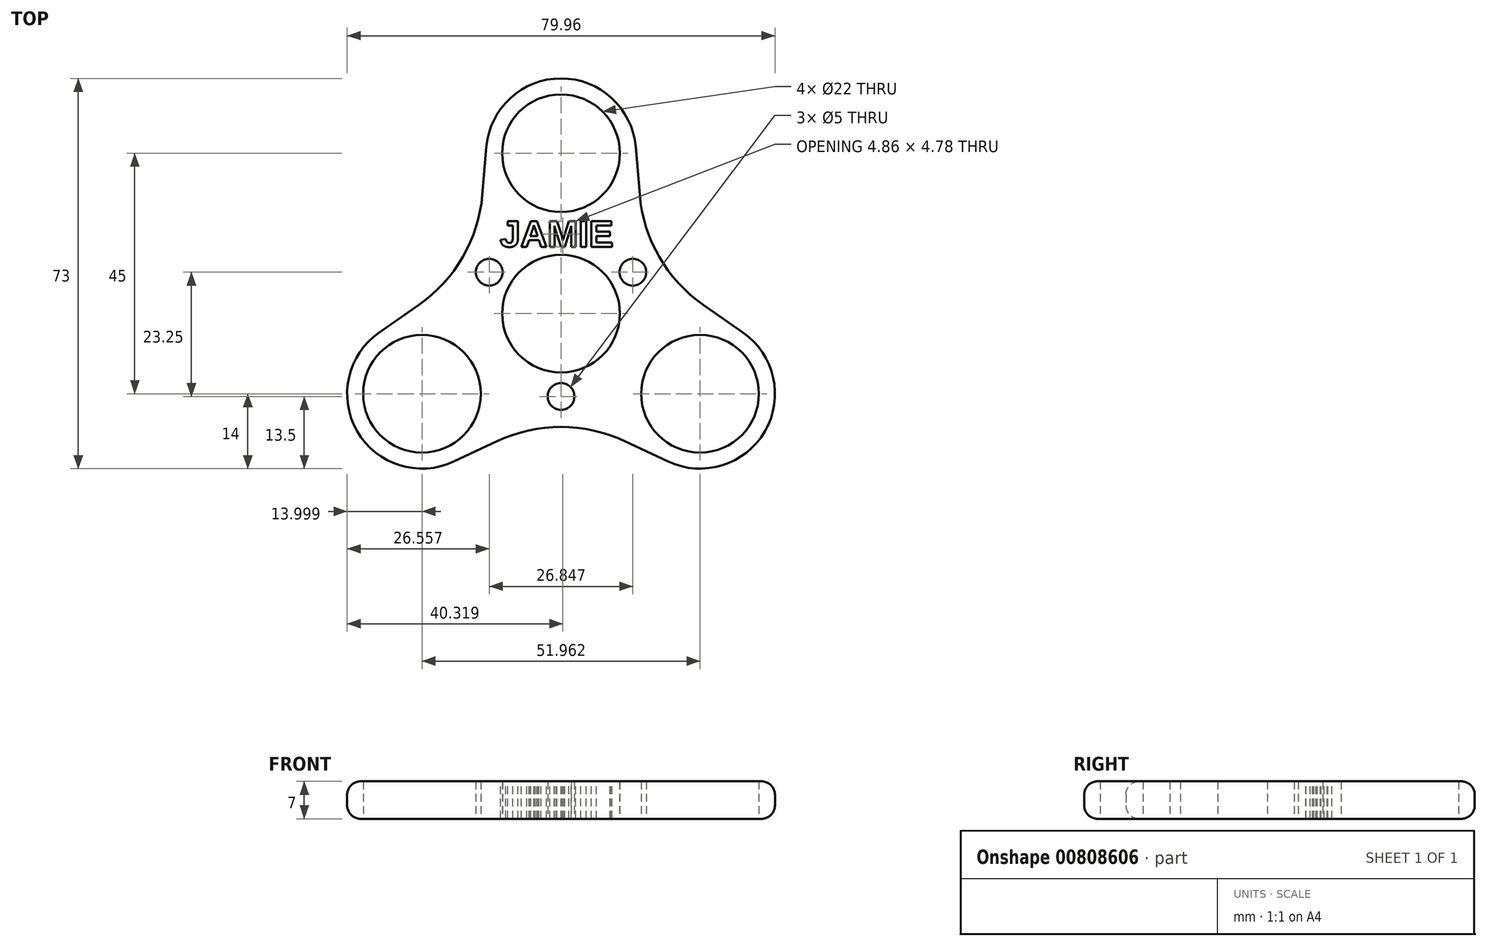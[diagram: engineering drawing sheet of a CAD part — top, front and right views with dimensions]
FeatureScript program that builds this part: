
annotation { "Feature Type Name" : "Feature", "Feature Type Description" : "" }
export const myFeature = defineFeature(function(context is Context, id is Id, definition is map)
    precondition{}
    {
        {
            var Q0;
            Q0=qCreatedBy(makeId("Top.planeOp"),FACE);
            var sketch = newSketch(context, id + "F0", { "sketchPlane" : qUnion([Q0])});
            skCircle(sketch, "E0", {"center": v(0, 0) * mm, "radius": 11 * mm});
            skLineSegment(sketch, "E1", {"start": v(0, 0) * mm, "end": v(0, 30) * mm});
            skCircle(sketch, "E2", {"center": v(0, 30) * mm, "radius": 11 * mm});
            skCircle(sketch, "E3", {"center": v(0, 30) * mm, "radius": 14 * mm});
            skLineSegment(sketch, "E4", {"start": v(0, 0) * mm, "end": v(-25.98, -15) * mm});
            skLineSegment(sketch, "E5", {"start": v(0, 0) * mm, "end": v(25.98, -15) * mm});
            skCircle(sketch, "E6", {"center": v(-25.98, -15) * mm, "radius": 11 * mm});
            skCircle(sketch, "E7", {"center": v(25.98, -15) * mm, "radius": 11 * mm});
            skCircle(sketch, "E8", {"center": v(25.98, -15) * mm, "radius": 14 * mm});
            skCircle(sketch, "E9", {"center": v(-25.98, -15) * mm, "radius": 14 * mm});
            skLineSegment(sketch, "E10", {"start": v(-56.74, -32.28) * mm, "end": v(-57.16, -33) * mm});
            skPoint(sketch, "E11.visualSharp", {"position": v(57.16, -33) * mm});
            skPoint(sketch, "E12.visualSharp", {"position": v(0, 66) * mm});
            skLineSegment(sketch, "E13", {"start": v(0, 0) * mm, "end": v(-13.42, 7.75) * mm});
            skCircle(sketch, "E14", {"center": v(-13.42, 7.75) * mm, "radius": 2.5 * mm});
            skLineSegment(sketch, "E15", {"start": v(-13.42, 7.75) * mm, "end": v(-15.59, 9) * mm});
            skLineSegment(sketch, "E16", {"start": v(-26.61, 1.62) * mm, "end": v(-33.98, -3.5) * mm});
            skLineSegment(sketch, "E17", {"start": v(-13.95, 31.18) * mm, "end": v(-14.7, 22.24) * mm});
            skPoint(sketch, "E18.orphan", {"position": v(-16.59, 0) * mm});
            skArc(sketch, "E19.filletArc", {"start": v(-26.61, 1.62) * mm, "mid": v(-18.36, 10.6) * mm, "end": v(-14.7, 22.24) * mm});
            skLineSegment(sketch, "E20", {"start": v(0, 0) * mm, "end": v(13.42, 7.75) * mm});
            skCircle(sketch, "E21", {"center": v(13.42, 7.75) * mm, "radius": 2.5 * mm});
            skLineSegment(sketch, "E22", {"start": v(13.95, 31.18) * mm, "end": v(14.7, 22.24) * mm});
            skLineSegment(sketch, "E23", {"start": v(33.98, -3.5) * mm, "end": v(26.61, 1.62) * mm});
            skArc(sketch, "E24.filletArc", {"start": v(14.7, 22.24) * mm, "mid": v(18.36, 10.6) * mm, "end": v(26.61, 1.62) * mm});
            skLineSegment(sketch, "E25", {"start": v(0, 0) * mm, "end": v(0, -15.5) * mm});
            skCircle(sketch, "E26", {"center": v(0, -15.5) * mm, "radius": 2.5 * mm});
            skLineSegment(sketch, "E27", {"start": v(-20.03, -27.67) * mm, "end": v(-11.9, -23.86) * mm});
            skLineSegment(sketch, "E28", {"start": v(20.03, -27.67) * mm, "end": v(11.9, -23.86) * mm});
            skArc(sketch, "E29.filletArc", {"start": v(11.9, -23.86) * mm, "mid": v(0, -21.2) * mm, "end": v(-11.9, -23.86) * mm});
            skSolve(sketch);
        }
        {
            var Q0;
            Q0 = qSketchRegion(id + "F0", true);
            extrude(context, id + "F1", {"entities" : qUnion([Q0]), "depth" : 7 * mm, "offsetDistance" : 25 * mm});
        }
        {
            var Q0;
            Q0=makeQuery(id+"F1.opExtrude","CAP_EDGE",EDGE,{"disambiguationData":[OSD([sQuery(id+"F0.wireOp",EDGE,"E24.filletArc")])],"isStart":false});
            var Q1;
            Q1=makeQuery(id+"F1.opExtrude","CAP_EDGE",EDGE,{"disambiguationData":[OSD([sQuery(id+"F0.wireOp",EDGE,"E19.filletArc")])],"isStart":true});
            fillet(context, id + "F2", {"entities" : qUnion([Q0, Q1]), "radius" : 2.5 * mm, "tangentPropagation" : true, "allowEdgeOverflow" : false});
        }
        {
            var Q0;
            Q0=makeQuery(id+"F1.opExtrude","CAP_FACE",FACE,{"disambiguationData":[OSD([sQuery(id+"F0.wireOp",EDGE,"E0"),sQuery(id+"F0.wireOp",EDGE,"E2"),sQuery(id+"F0.wireOp",EDGE,"E3"),sQuery(id+"F0.wireOp",EDGE,"E6"),sQuery(id+"F0.wireOp",EDGE,"E7"),sQuery(id+"F0.wireOp",EDGE,"E8"),sQuery(id+"F0.wireOp",EDGE,"E9"),sQuery(id+"F0.wireOp",EDGE,"E14"),sQuery(id+"F0.wireOp",EDGE,"E16"),sQuery(id+"F0.wireOp",EDGE,"E17"),sQuery(id+"F0.wireOp",EDGE,"E19.filletArc"),sQuery(id+"F0.wireOp",EDGE,"E21"),sQuery(id+"F0.wireOp",EDGE,"E22"),sQuery(id+"F0.wireOp",EDGE,"E23"),sQuery(id+"F0.wireOp",EDGE,"E24.filletArc"),sQuery(id+"F0.wireOp",EDGE,"E26"),sQuery(id+"F0.wireOp",EDGE,"E27"),sQuery(id+"F0.wireOp",EDGE,"E28"),sQuery(id+"F0.wireOp",EDGE,"E29.filletArc")])],"isStart":false});
            var sketch = newSketch(context, id + "F3", { "sketchPlane" : qUnion([Q0])});
            skText(sketch, "E30", { "text": "JAMIE", "fontName": "Arimo-Bold.ttf"});
            const initialGuessF3  = {"E30": [-0.01143, 0.0125, 1, 0, 0.005]};
            skSetInitialGuess(sketch, initialGuessF3);
            skSolve(sketch);
        }
        {
            var Q0;
            Q0 = qSketchRegion(id + "F3", true);
            extrude(context, id + "F4", {"entities" : qUnion([Q0]), "operationType" : NewBodyOperationType.REMOVE, "oppositeDirection" : true, "depth" : 8 * mm, "offsetDistance" : 25 * mm});
        }
    });
